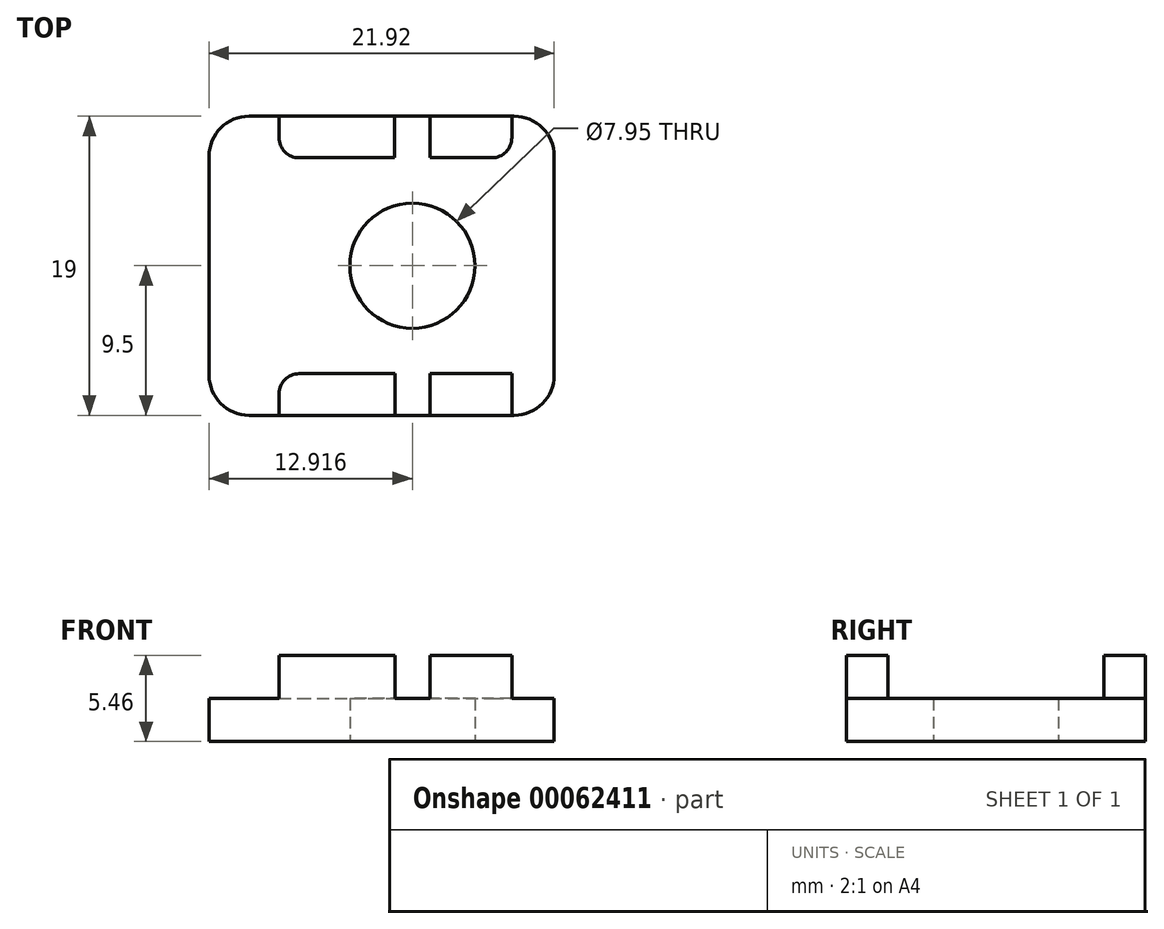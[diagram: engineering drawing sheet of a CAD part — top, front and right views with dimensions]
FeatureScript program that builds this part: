
annotation { "Feature Type Name" : "Feature", "Feature Type Description" : "" }
export const myFeature = defineFeature(function(context is Context, id is Id, definition is map)
    precondition{}
    {
        {
            var Q0;
            Q0=qCreatedBy(makeId("Top.planeOp"),FACE);
            var sketch = newSketch(context, id + "F0", { "sketchPlane" : qUnion([Q0])});
            skLineSegment(sketch, "E0.rect.bottom", {"start": v(-8.42, 9.5) * mm, "end": v(8.42, 9.5) * mm});
            skLineSegment(sketch, "E0.rect.top", {"start": v(-8.42, -9.5) * mm, "end": v(8.42, -9.5) * mm});
            skLineSegment(sketch, "E0.rect.left", {"start": v(-10.96, 6.96) * mm, "end": v(-10.96, -6.96) * mm});
            skLineSegment(sketch, "E0.rect.right", {"start": v(10.96, 6.96) * mm, "end": v(10.96, -6.96) * mm});
            skPoint(sketch, "E0.rect.middle", {"position": v(0, 0) * mm});
            skCircle(sketch, "E1", {"center": v(1.96, 0) * mm, "radius": 3.98 * mm});
            skPoint(sketch, "E2.visualSharp", {"position": v(-10.96, 9.5) * mm});
            skArc(sketch, "E2.filletArc", {"start": v(-8.42, 9.5) * mm, "mid": v(-10.22, 8.76) * mm, "end": v(-10.96, 6.96) * mm});
            skPoint(sketch, "E3.visualSharp", {"position": v(-10.96, -9.5) * mm});
            skArc(sketch, "E3.filletArc", {"start": v(-10.96, -6.96) * mm, "mid": v(-10.22, -8.76) * mm, "end": v(-8.42, -9.5) * mm});
            skPoint(sketch, "E4.visualSharp", {"position": v(10.96, -9.5) * mm});
            skArc(sketch, "E4.filletArc", {"start": v(8.42, -9.5) * mm, "mid": v(10.22, -8.76) * mm, "end": v(10.96, -6.96) * mm});
            skPoint(sketch, "E5.visualSharp", {"position": v(10.96, 9.5) * mm});
            skArc(sketch, "E5.filletArc", {"start": v(10.96, 6.96) * mm, "mid": v(10.22, 8.76) * mm, "end": v(8.42, 9.5) * mm});
            skSolve(sketch);
        }
        {
            var Q0;
            Q0 = qSketchRegion(id + "F0", true);
            extrude(context, id + "F1", {"entities" : qUnion([Q0]), "depth" : 2.72 * mm});
        }
        {
            var Q0;
            Q0=makeQuery(id+"F1.opExtrude","CAP_FACE",FACE,{"disambiguationData":[OSD([sQuery(id+"F0.wireOp",EDGE,"E0.rect.bottom"),sQuery(id+"F0.wireOp",EDGE,"E0.rect.top"),sQuery(id+"F0.wireOp",EDGE,"E0.rect.left"),sQuery(id+"F0.wireOp",EDGE,"E0.rect.right"),sQuery(id+"F0.wireOp",EDGE,"f2b5ce7b-4114-4757-a126-e494b4b68391")])],"isStart":false});
            var sketch = newSketch(context, id + "F2", { "sketchPlane" : qUnion([Q0])});
            skLineSegment(sketch, "E6.bottom", {"start": v(-6.52, 9.5) * mm, "end": v(0.83, 9.5) * mm});
            skLineSegment(sketch, "E6.top", {"start": v(-5.25, 6.86) * mm, "end": v(0.83, 6.86) * mm});
            skLineSegment(sketch, "E6.left", {"start": v(-6.52, 9.5) * mm, "end": v(-6.52, 8.13) * mm});
            skLineSegment(sketch, "E6.right", {"start": v(0.83, 9.5) * mm, "end": v(0.83, 6.86) * mm});
            skPoint(sketch, "E7.visualSharp", {"position": v(-6.52, 6.86) * mm});
            skArc(sketch, "E7.filletArc", {"start": v(-6.52, 8.13) * mm, "mid": v(-6.14, 7.23) * mm, "end": v(-5.25, 6.86) * mm});
            skLineSegment(sketch, "E8.bottom", {"start": v(3.06, 9.5) * mm, "end": v(8.27, 9.5) * mm});
            skLineSegment(sketch, "E8.top", {"start": v(3.06, 6.86) * mm, "end": v(7, 6.86) * mm});
            skLineSegment(sketch, "E8.left", {"start": v(3.06, 9.5) * mm, "end": v(3.06, 6.86) * mm});
            skLineSegment(sketch, "E8.right", {"start": v(8.27, 9.5) * mm, "end": v(8.27, 8.13) * mm});
            skPoint(sketch, "E9.visualSharp", {"position": v(8.27, 6.86) * mm});
            skArc(sketch, "E9.filletArc", {"start": v(7, 6.86) * mm, "mid": v(7.9, 7.23) * mm, "end": v(8.27, 8.13) * mm});
            skLineSegment(sketch, "E10.bottom", {"start": v(-6.52, -9.5) * mm, "end": v(0.84, -9.5) * mm});
            skLineSegment(sketch, "E10.top", {"start": v(-5.25, -6.86) * mm, "end": v(0.84, -6.86) * mm});
            skLineSegment(sketch, "E10.left", {"start": v(-6.52, -9.5) * mm, "end": v(-6.52, -8.13) * mm});
            skLineSegment(sketch, "E10.right", {"start": v(0.84, -9.5) * mm, "end": v(0.84, -6.86) * mm});
            skArc(sketch, "E11.filletArc", {"start": v(-5.25, -6.86) * mm, "mid": v(-6.14, -7.23) * mm, "end": v(-6.52, -8.13) * mm});
            skLineSegment(sketch, "E12.bottom", {"start": v(8.27, -9.5) * mm, "end": v(3.06, -9.5) * mm});
            skLineSegment(sketch, "E12.top", {"start": v(8.27, -6.86) * mm, "end": v(3.06, -6.86) * mm});
            skLineSegment(sketch, "E12.left", {"start": v(8.27, -9.5) * mm, "end": v(8.27, -6.86) * mm});
            skLineSegment(sketch, "E12.right", {"start": v(3.06, -9.5) * mm, "end": v(3.06, -6.86) * mm});
            skPoint(sketch, "E13.visualSharp", {"position": v(8.27, -6.86) * mm});
            skLineSegment(sketch, "E13.filletArc", {"start": v(8.27, -6.86) * mm, "end": v(8.27, -6.86) * mm});
            skSolve(sketch);
        }
        {
            var Q0;
            Q0 = qSketchRegion(id + "F2", true);
            extrude(context, id + "F3", {"entities" : qUnion([Q0]), "operationType" : NewBodyOperationType.ADD, "depth" : 2.74 * mm});
        }
    });
